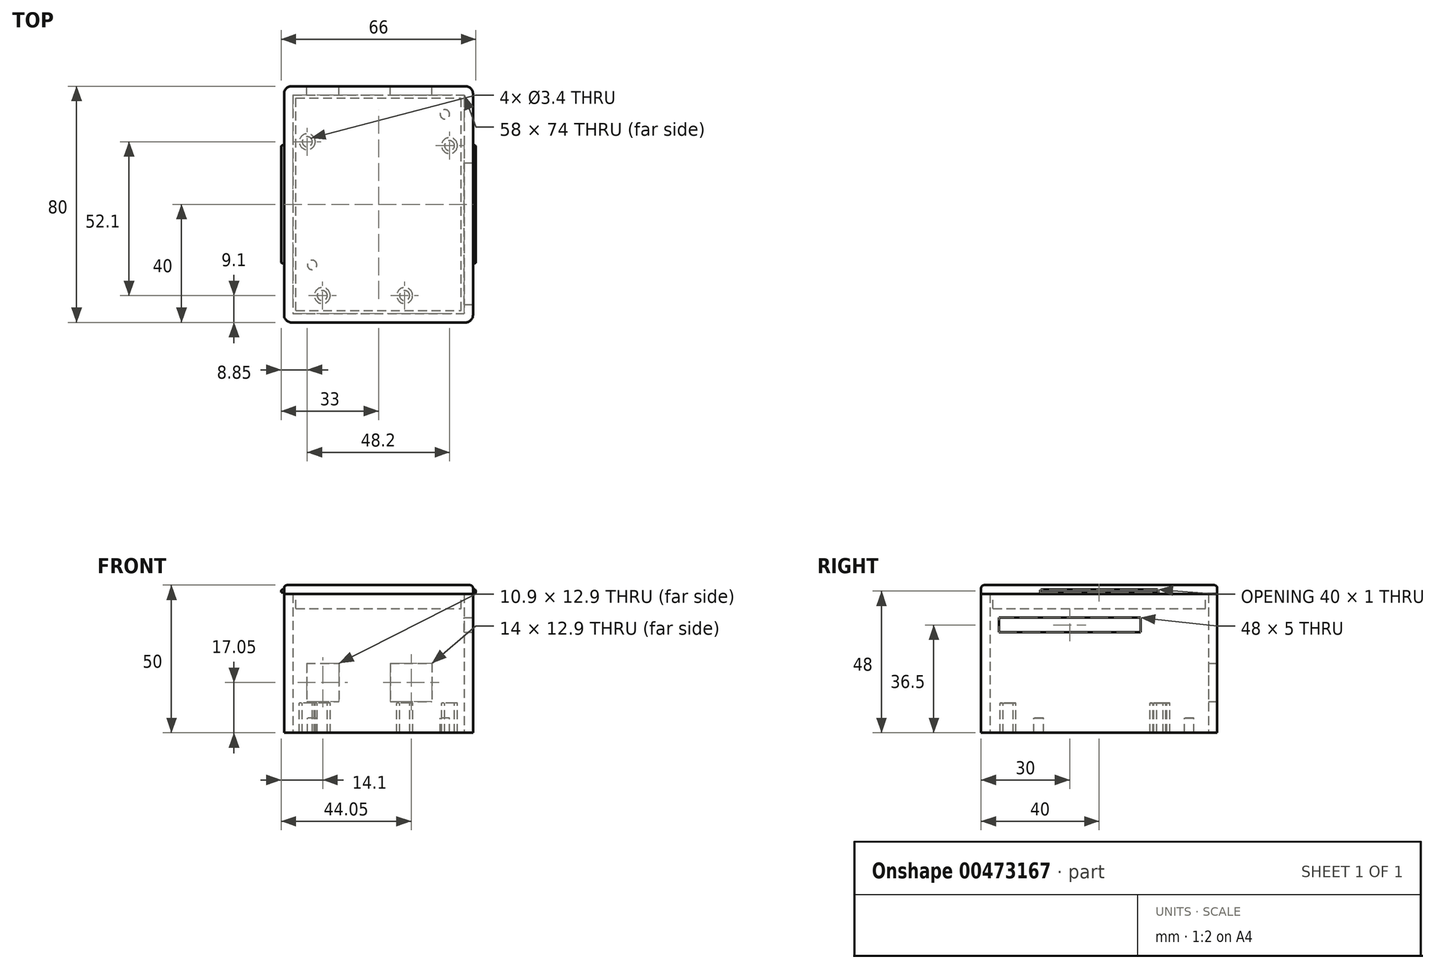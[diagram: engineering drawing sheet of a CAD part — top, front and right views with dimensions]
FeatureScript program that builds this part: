
annotation { "Feature Type Name" : "Feature", "Feature Type Description" : "" }
export const myFeature = defineFeature(function(context is Context, id is Id, definition is map)
    precondition{}
    {
        {
            var Q0;
            Q0=qCreatedBy(makeId("Top.planeOp"),FACE);
            var sketch = newSketch(context, id + "F0", { "sketchPlane" : qUnion([Q0])});
            skLineSegment(sketch, "E0.bottom", {"start": v(-32, 40) * mm, "end": v(32, 40) * mm});
            skLineSegment(sketch, "E0.top", {"start": v(-32, -40) * mm, "end": v(32, -40) * mm});
            skLineSegment(sketch, "E0.left", {"start": v(-32, 40) * mm, "end": v(-32, -40) * mm});
            skLineSegment(sketch, "E0.right", {"start": v(32, 40) * mm, "end": v(32, -40) * mm});
            skPoint(sketch, "E0.middle", {"position": v(0, 0) * mm});
            skSolve(sketch);
        }
        {
            var Q0;
            Q0=makeQuery(id+"F0.imprint","IMPRINT",FACE,{"disambiguationData":[TD([[makeQuery(id+"F0.imprint","IMPRINT",EDGE,{"derivedFrom":sQuery(id+"F0.wireOp",EDGE,"E0.bottom")}),-1.0]])]});
            extrude(context, id + "F1", {"entities" : qUnion([Q0]), "depth" : 45 * mm});
        }
        {
            var Q0;
            Q0=makeQuery(id+"F1.opExtrude","CAP_FACE",FACE,{"disambiguationData":[OSD([sQuery(id+"F0.wireOp",EDGE,"E0.bottom"),sQuery(id+"F0.wireOp",EDGE,"E0.top"),sQuery(id+"F0.wireOp",EDGE,"E0.left"),sQuery(id+"F0.wireOp",EDGE,"E0.right")])],"isStart":false});
            shell(context, id + "F2", {"entities" : qUnion([Q0]), "thickness" : 3 * mm});
        }
        {
            var Q0;
            Q0=makeQuery(id+"F1.opExtrude","CAP_FACE",FACE,{"disambiguationData":[OSD([sQuery(id+"F0.wireOp",EDGE,"E0.bottom"),sQuery(id+"F0.wireOp",EDGE,"E0.top"),sQuery(id+"F0.wireOp",EDGE,"E0.left"),sQuery(id+"F0.wireOp",EDGE,"E0.right")])],"isStart":true});
            extrude(context, id + "F3", {"entities" : qUnion([Q0]), "operationType" : NewBodyOperationType.ADD, "depth" : 2 * mm});
        }
        {
            var Q0;
            Q0=makeQuery(id+"F1.opExtrude","CAP_FACE",FACE,{"disambiguationData":[OSD([sQuery(id+"F0.wireOp",EDGE,"E0.bottom"),sQuery(id+"F0.wireOp",EDGE,"E0.top"),sQuery(id+"F0.wireOp",EDGE,"E0.left"),sQuery(id+"F0.wireOp",EDGE,"E0.right")])],"isStart":false});
            var sketch = newSketch(context, id + "F4", { "sketchPlane" : qUnion([Q0])});
            skLineSegment(sketch, "E1.bottom", {"start": v(-32, 40) * mm, "end": v(32, 40) * mm});
            skLineSegment(sketch, "E1.top", {"start": v(-32, -40) * mm, "end": v(32, -40) * mm});
            skLineSegment(sketch, "E1.left", {"start": v(-32, 40) * mm, "end": v(-32, -40) * mm});
            skLineSegment(sketch, "E1.right", {"start": v(32, 40) * mm, "end": v(32, -40) * mm});
            skLineSegment(sketch, "E2.bottom", {"start": v(-28, -36) * mm, "end": v(28, -36) * mm});
            skLineSegment(sketch, "E2.top", {"start": v(-28, 36) * mm, "end": v(28, 36) * mm});
            skLineSegment(sketch, "E2.left", {"start": v(-28, -36) * mm, "end": v(-28, 36) * mm});
            skLineSegment(sketch, "E2.right", {"start": v(28, -36) * mm, "end": v(28, 36) * mm});
            skPoint(sketch, "E2.middle", {"position": v(0, 0) * mm});
            skSolve(sketch);
        }
        {
            var Q0;
            Q0=makeQuery(id+"F4.imprint","IMPRINT",FACE,{"disambiguationData":[TD([[makeQuery(id+"F4.imprint","IMPRINT",EDGE,{"derivedFrom":sQuery(id+"F4.wireOp",EDGE,"E1.bottom")}),-1.0]])]});
            var Q1;
            Q1=makeQuery(id+"F4.imprint","IMPRINT",FACE,{"disambiguationData":[TD([[makeQuery(id+"F4.imprint","IMPRINT",EDGE,{"derivedFrom":sQuery(id+"F4.wireOp",EDGE,"E2.bottom")}),-1.0]])]});
            var Q2;
            Q2=makeQuery(id+"F4.imprint","IMPRINT",FACE,{"disambiguationData":[TD([[makeQuery(id+"F4.imprint","IMPRINT",EDGE,{"derivedFrom":sQuery(id+"F4.wireOp",EDGE,"E2.bottom")}),1.0]])]});
            extrude(context, id + "F5", {"entities" : qUnion([Q0, Q1, Q2]), "depth" : 3 * mm});
        }
        {
            var Q0;
            Q0=makeQuery(id+"F4.imprint","IMPRINT",FACE,{"disambiguationData":[TD([[makeQuery(id+"F4.imprint","IMPRINT",EDGE,{"derivedFrom":sQuery(id+"F4.wireOp",EDGE,"E2.bottom")}),1.0]])]});
            extrude(context, id + "F6", {"entities" : qUnion([Q0]), "operationType" : NewBodyOperationType.ADD, "oppositeDirection" : true, "depth" : 5 * mm, "offsetDistance" : 25 * mm});
        }
        {
            var Q0;
            Q0=makeQuery(id+"F2.opShell","OFFSET_FACE",FACE,{"disambiguationData":[OSD([sQuery(id+"F0.wireOp",EDGE,"E0.bottom"),sQuery(id+"F0.wireOp",EDGE,"E0.top"),sQuery(id+"F0.wireOp",EDGE,"E0.left"),sQuery(id+"F0.wireOp",EDGE,"E0.right")])]});
            var sketch = newSketch(context, id + "F7", { "sketchPlane" : qUnion([Q0])});
            skCircle(sketch, "E3", {"center": v(8.85, -30.9) * mm, "radius": 1.7 * mm});
            skCircle(sketch, "E4", {"center": v(-19.05, -30.9) * mm, "radius": 1.7 * mm});
            skCircle(sketch, "E5", {"center": v(-24.15, 21.2) * mm, "radius": 1.7 * mm});
            skCircle(sketch, "E6", {"center": v(24.05, 19.9) * mm, "radius": 1.7 * mm});
            skCircle(sketch, "E7", {"center": v(-24.15, 21.2) * mm, "radius": 2.7 * mm});
            skCircle(sketch, "E8", {"center": v(24.05, 19.9) * mm, "radius": 2.7 * mm});
            skCircle(sketch, "E9", {"center": v(-19.05, -30.9) * mm, "radius": 2.7 * mm});
            skCircle(sketch, "E10", {"center": v(8.85, -30.9) * mm, "radius": 2.7 * mm});
            skCircle(sketch, "E11", {"center": v(22.5, -20.5) * mm, "radius": 1.6 * mm});
            skCircle(sketch, "E12.MirrorC", {"center": v(-22.5, -20.5) * mm, "radius": 1.6 * mm});
            skCircle(sketch, "E13", {"center": v(-22.5, 30.5) * mm, "radius": 1.6 * mm});
            skCircle(sketch, "E14.MirrorC", {"center": v(22.5, 30.5) * mm, "radius": 1.6 * mm});
            skLineSegment(sketch, "E15", {"start": v(24.05, 19.9) * mm, "end": v(-4.37, 19.9) * mm, "construction": true});
            skLineSegment(sketch, "E16", {"start": v(-24.15, 21.2) * mm, "end": v(-24.15, -16.15) * mm, "construction": true});
            skLineSegment(sketch, "E17", {"start": v(8.85, -30.9) * mm, "end": v(8.85, -1.88) * mm, "construction": true});
            skSolve(sketch);
        }
        {
            var Q0;
            Q0=makeQuery(id+"F7.imprint","IMPRINT",FACE,{"disambiguationData":[TD([[makeQuery(id+"F7.imprint","IMPRINT",EDGE,{"derivedFrom":sQuery(id+"F7.wireOp",EDGE,"E3")}),-1.0]])]});
            var Q1;
            Q1=makeQuery(id+"F7.imprint","IMPRINT",FACE,{"disambiguationData":[TD([[makeQuery(id+"F7.imprint","IMPRINT",EDGE,{"derivedFrom":sQuery(id+"F7.wireOp",EDGE,"E4")}),-1.0]])]});
            var Q2;
            Q2=makeQuery(id+"F7.imprint","IMPRINT",FACE,{"disambiguationData":[TD([[makeQuery(id+"F7.imprint","IMPRINT",EDGE,{"derivedFrom":sQuery(id+"F7.wireOp",EDGE,"E5")}),-1.0]])]});
            var Q3;
            Q3=makeQuery(id+"F7.imprint","IMPRINT",FACE,{"disambiguationData":[TD([[makeQuery(id+"F7.imprint","IMPRINT",EDGE,{"derivedFrom":sQuery(id+"F7.wireOp",EDGE,"E6")}),-1.0]])]});
            extrude(context, id + "F8", {"entities" : qUnion([Q0, Q1, Q2, Q3]), "operationType" : NewBodyOperationType.ADD, "depth" : 5 * mm});
        }
        {
            var Q0;
            Q0=makeQuery(id+"F8.boolean.opBoolean","SPLIT",FACE,{"disambiguationData":[TD([makeQuery(id+"F8.opExtrude","SWEPT_FACE",FACE,{"disambiguationData":[OSD([sQuery(id+"F7.wireOp",EDGE,"E5")])]})])],"derivedFrom":makeQuery(id+"F2.opShell","OFFSET_FACE",FACE,{"disambiguationData":[OSD([sQuery(id+"F0.wireOp",EDGE,"E0.bottom"),sQuery(id+"F0.wireOp",EDGE,"E0.top"),sQuery(id+"F0.wireOp",EDGE,"E0.left"),sQuery(id+"F0.wireOp",EDGE,"E0.right")])]})});
            var Q1;
            Q1=makeQuery(id+"F8.boolean.opBoolean","SPLIT",FACE,{"disambiguationData":[TD([makeQuery(id+"F8.opExtrude","SWEPT_FACE",FACE,{"disambiguationData":[OSD([sQuery(id+"F7.wireOp",EDGE,"E6")])]})])],"derivedFrom":makeQuery(id+"F2.opShell","OFFSET_FACE",FACE,{"disambiguationData":[OSD([sQuery(id+"F0.wireOp",EDGE,"E0.bottom"),sQuery(id+"F0.wireOp",EDGE,"E0.top"),sQuery(id+"F0.wireOp",EDGE,"E0.left"),sQuery(id+"F0.wireOp",EDGE,"E0.right")])]})});
            var Q2;
            Q2=makeQuery(id+"F8.boolean.opBoolean","SPLIT",FACE,{"disambiguationData":[TD([makeQuery(id+"F8.opExtrude","SWEPT_FACE",FACE,{"disambiguationData":[OSD([sQuery(id+"F7.wireOp",EDGE,"E3")])]})])],"derivedFrom":makeQuery(id+"F2.opShell","OFFSET_FACE",FACE,{"disambiguationData":[OSD([sQuery(id+"F0.wireOp",EDGE,"E0.bottom"),sQuery(id+"F0.wireOp",EDGE,"E0.top"),sQuery(id+"F0.wireOp",EDGE,"E0.left"),sQuery(id+"F0.wireOp",EDGE,"E0.right")])]})});
            var Q3;
            Q3=makeQuery(id+"F8.boolean.opBoolean","SPLIT",FACE,{"disambiguationData":[TD([makeQuery(id+"F8.opExtrude","SWEPT_FACE",FACE,{"disambiguationData":[OSD([sQuery(id+"F7.wireOp",EDGE,"E4")])]})])],"derivedFrom":makeQuery(id+"F2.opShell","OFFSET_FACE",FACE,{"disambiguationData":[OSD([sQuery(id+"F0.wireOp",EDGE,"E0.bottom"),sQuery(id+"F0.wireOp",EDGE,"E0.top"),sQuery(id+"F0.wireOp",EDGE,"E0.left"),sQuery(id+"F0.wireOp",EDGE,"E0.right")])]})});
            var Q4;
            Q4=makeQuery(id+"F7.imprint","IMPRINT",FACE,{"disambiguationData":[TD([[makeQuery(id+"F7.imprint","IMPRINT",EDGE,{"derivedFrom":sQuery(id+"F7.wireOp",EDGE,"E13")}),1.0]])]});
            var Q5;
            Q5=makeQuery(id+"F7.imprint","IMPRINT",FACE,{"disambiguationData":[TD([[makeQuery(id+"F7.imprint","IMPRINT",EDGE,{"derivedFrom":sQuery(id+"F7.wireOp",EDGE,"E14.MirrorC")}),-1.0]])]});
            var Q6;
            Q6=makeQuery(id+"F7.imprint","IMPRINT",FACE,{"disambiguationData":[TD([[makeQuery(id+"F7.imprint","IMPRINT",EDGE,{"derivedFrom":sQuery(id+"F7.wireOp",EDGE,"E11")}),1.0]])]});
            var Q7;
            Q7=makeQuery(id+"F7.imprint","IMPRINT",FACE,{"disambiguationData":[TD([[makeQuery(id+"F7.imprint","IMPRINT",EDGE,{"derivedFrom":sQuery(id+"F7.wireOp",EDGE,"E12.MirrorC")}),-1.0]])]});
            extrude(context, id + "F9", {"entities" : qUnion([Q0, Q1, Q2, Q3, Q4, Q5, Q6, Q7]), "operationType" : NewBodyOperationType.REMOVE, "oppositeDirection" : true, "depth" : 5 * mm});
        }
        {
            var Q0;
            Q0=makeQuery(id+"F3.opExtrude","CAP_FACE",FACE,{"disambiguationData":[OSD([sQuery(id+"F0.wireOp",EDGE,"E0.bottom"),sQuery(id+"F0.wireOp",EDGE,"E0.top"),sQuery(id+"F0.wireOp",EDGE,"E0.left"),sQuery(id+"F0.wireOp",EDGE,"E0.right")])],"isStart":false});
            var sketch = newSketch(context, id + "F10", { "sketchPlane" : qUnion([Q0])});
            skCircle(sketch, "E18", {"center": v(-19.05, 30.9) * mm, "radius": 2.73 * mm});
            skCircle(sketch, "E19", {"center": v(8.85, 30.9) * mm, "radius": 2.73 * mm});
            skCircle(sketch, "E20.cCircle", {"center": v(-19.05, 30.9) * mm, "radius": 2.73 * mm, "construction": true});
            skLineSegment(sketch, "E20.0", {"start": v(-17.48, 28.17) * mm, "end": v(-20.63, 28.17) * mm});
            skLineSegment(sketch, "E20.1", {"start": v(-20.63, 28.17) * mm, "end": v(-22.2, 30.9) * mm});
            skLineSegment(sketch, "E20.2", {"start": v(-22.2, 30.9) * mm, "end": v(-20.63, 33.63) * mm});
            skLineSegment(sketch, "E20.3", {"start": v(-20.63, 33.63) * mm, "end": v(-17.48, 33.63) * mm});
            skLineSegment(sketch, "E20.4", {"start": v(-17.48, 33.63) * mm, "end": v(-15.9, 30.9) * mm});
            skLineSegment(sketch, "E20.5", {"start": v(-15.9, 30.9) * mm, "end": v(-17.48, 28.17) * mm});
            skPoint(sketch, "E20.0.midPoint", {"position": v(-19.05, 28.17) * mm});
            skCircle(sketch, "E21.cCircle", {"center": v(8.85, 30.9) * mm, "radius": 2.73 * mm, "construction": true});
            skLineSegment(sketch, "E21.0", {"start": v(10.42, 28.17) * mm, "end": v(7.27, 28.17) * mm});
            skLineSegment(sketch, "E21.1", {"start": v(7.27, 28.17) * mm, "end": v(5.7, 30.9) * mm});
            skLineSegment(sketch, "E21.2", {"start": v(5.7, 30.9) * mm, "end": v(7.27, 33.63) * mm});
            skLineSegment(sketch, "E21.3", {"start": v(7.27, 33.63) * mm, "end": v(10.42, 33.63) * mm});
            skLineSegment(sketch, "E21.4", {"start": v(10.42, 33.63) * mm, "end": v(12, 30.9) * mm});
            skLineSegment(sketch, "E21.5", {"start": v(12, 30.9) * mm, "end": v(10.42, 28.17) * mm});
            skPoint(sketch, "E21.0.midPoint", {"position": v(8.85, 28.17) * mm});
            skCircle(sketch, "E22", {"center": v(-24.15, -21.2) * mm, "radius": 2.73 * mm});
            skCircle(sketch, "E23", {"center": v(24.05, -19.9) * mm, "radius": 2.73 * mm});
            skCircle(sketch, "E24.cCircle", {"center": v(-24.15, -21.2) * mm, "radius": 2.73 * mm, "construction": true});
            skLineSegment(sketch, "E24.0", {"start": v(-22.58, -23.93) * mm, "end": v(-25.73, -23.93) * mm});
            skLineSegment(sketch, "E24.1", {"start": v(-25.73, -23.93) * mm, "end": v(-27.3, -21.2) * mm});
            skLineSegment(sketch, "E24.2", {"start": v(-27.3, -21.2) * mm, "end": v(-25.73, -18.47) * mm});
            skLineSegment(sketch, "E24.3", {"start": v(-25.73, -18.47) * mm, "end": v(-22.58, -18.47) * mm});
            skLineSegment(sketch, "E24.4", {"start": v(-22.58, -18.47) * mm, "end": v(-21, -21.2) * mm});
            skLineSegment(sketch, "E24.5", {"start": v(-21, -21.2) * mm, "end": v(-22.58, -23.93) * mm});
            skPoint(sketch, "E24.0.midPoint", {"position": v(-24.15, -23.93) * mm});
            skCircle(sketch, "E25.cCircle", {"center": v(24.05, -19.9) * mm, "radius": 2.73 * mm, "construction": true});
            skLineSegment(sketch, "E25.0", {"start": v(25.62, -22.63) * mm, "end": v(22.47, -22.63) * mm});
            skLineSegment(sketch, "E25.1", {"start": v(22.47, -22.63) * mm, "end": v(20.9, -19.9) * mm});
            skLineSegment(sketch, "E25.2", {"start": v(20.9, -19.9) * mm, "end": v(22.47, -17.17) * mm});
            skLineSegment(sketch, "E25.3", {"start": v(22.47, -17.17) * mm, "end": v(25.62, -17.17) * mm});
            skLineSegment(sketch, "E25.4", {"start": v(25.62, -17.17) * mm, "end": v(27.2, -19.9) * mm});
            skLineSegment(sketch, "E25.5", {"start": v(27.2, -19.9) * mm, "end": v(25.62, -22.63) * mm});
            skPoint(sketch, "E25.0.midPoint", {"position": v(24.05, -22.63) * mm});
            skSolve(sketch);
        }
        {
            var Q0;
            Q0=makeQuery(id+"F10.imprint","IMPRINT",FACE,{"disambiguationData":[TD([[makeQuery(id+"F10.imprint","IMPRINT",EDGE,{"derivedFrom":makeQuery(id+"F9.boolean.opBoolean","COPY",EDGE,{"derivedFrom":makeQuery(id+"F9.opExtrude","CAP_EDGE",EDGE,{"disambiguationData":[OSD([sQuery(id+"F7.wireOp",EDGE,"E4")])],"isStart":false})})}),1.0]])]});
            var Q1;
            {var subQ0=sQuery(id+"F10.wireOp",EDGE,"E20.3");var subQ1=sQuery(id+"F10.wireOp",EDGE,"E18");var subQ2=makeQuery(id+"F10.imprint","INTERSECT",VERTEX,{"derivedFrom":[subQ1,subQ0]});Q1=makeQuery(id+"F10.imprint","IMPRINT",FACE,{"disambiguationData":[TD([[makeQuery(id+"F10.imprint","IMPRINT",EDGE,{"disambiguationData":[TD([[subQ2,-1.0]])],"derivedFrom":subQ1}),-1.0]])]});}
            var Q2;
            {var subQ0=sQuery(id+"F10.wireOp",EDGE,"E20.2");var subQ1=sQuery(id+"F10.wireOp",EDGE,"E18");var subQ2=makeQuery(id+"F10.imprint","INTERSECT",VERTEX,{"derivedFrom":[subQ1,subQ0]});Q2=makeQuery(id+"F10.imprint","IMPRINT",FACE,{"disambiguationData":[TD([[makeQuery(id+"F10.imprint","IMPRINT",EDGE,{"disambiguationData":[TD([[subQ2,-1.0]])],"derivedFrom":subQ1}),-1.0]])]});}
            var Q3;
            {var subQ0=sQuery(id+"F10.wireOp",EDGE,"E20.1");var subQ1=sQuery(id+"F10.wireOp",EDGE,"E18");var subQ2=makeQuery(id+"F10.imprint","INTERSECT",VERTEX,{"derivedFrom":[subQ1,subQ0]});Q3=makeQuery(id+"F10.imprint","IMPRINT",FACE,{"disambiguationData":[TD([[makeQuery(id+"F10.imprint","IMPRINT",EDGE,{"disambiguationData":[TD([[subQ2,-1.0]])],"derivedFrom":subQ1}),-1.0]])]});}
            var Q4;
            {var subQ0=sQuery(id+"F10.wireOp",EDGE,"E20.0");var subQ1=sQuery(id+"F10.wireOp",EDGE,"E18");var subQ2=makeQuery(id+"F10.imprint","INTERSECT",VERTEX,{"derivedFrom":[subQ1,subQ0]});Q4=makeQuery(id+"F10.imprint","IMPRINT",FACE,{"disambiguationData":[TD([[makeQuery(id+"F10.imprint","IMPRINT",EDGE,{"disambiguationData":[TD([[subQ2,-1.0]])],"derivedFrom":subQ1}),-1.0]])]});}
            var Q5;
            {var subQ0=sQuery(id+"F10.wireOp",EDGE,"E20.4");var subQ1=sQuery(id+"F10.wireOp",EDGE,"E18");var subQ2=makeQuery(id+"F10.imprint","INTERSECT",VERTEX,{"derivedFrom":[subQ1,subQ0]});Q5=makeQuery(id+"F10.imprint","IMPRINT",FACE,{"disambiguationData":[TD([[makeQuery(id+"F10.imprint","IMPRINT",EDGE,{"disambiguationData":[TD([[subQ2,1.0]])],"derivedFrom":subQ1}),-1.0]])]});}
            var Q6;
            {var subQ0=sQuery(id+"F10.wireOp",EDGE,"E20.3");var subQ1=sQuery(id+"F10.wireOp",EDGE,"E18");var subQ2=makeQuery(id+"F10.imprint","INTERSECT",VERTEX,{"derivedFrom":[subQ1,subQ0]});Q6=makeQuery(id+"F10.imprint","IMPRINT",FACE,{"disambiguationData":[TD([[makeQuery(id+"F10.imprint","IMPRINT",EDGE,{"disambiguationData":[TD([[subQ2,1.0]])],"derivedFrom":subQ1}),-1.0]])]});}
            var Q7;
            Q7=makeQuery(id+"F10.imprint","IMPRINT",FACE,{"disambiguationData":[TD([[makeQuery(id+"F10.imprint","IMPRINT",EDGE,{"derivedFrom":makeQuery(id+"F9.boolean.opBoolean","COPY",EDGE,{"derivedFrom":makeQuery(id+"F9.opExtrude","CAP_EDGE",EDGE,{"disambiguationData":[OSD([sQuery(id+"F7.wireOp",EDGE,"E3")])],"isStart":false})})}),1.0]])]});
            var Q8;
            {var subQ0=sQuery(id+"F10.wireOp",EDGE,"E21.3");var subQ1=sQuery(id+"F10.wireOp",EDGE,"E19");var subQ2=makeQuery(id+"F10.imprint","INTERSECT",VERTEX,{"derivedFrom":[subQ1,subQ0]});Q8=makeQuery(id+"F10.imprint","IMPRINT",FACE,{"disambiguationData":[TD([[makeQuery(id+"F10.imprint","IMPRINT",EDGE,{"disambiguationData":[TD([[subQ2,-1.0]])],"derivedFrom":subQ1}),-1.0]])]});}
            var Q9;
            {var subQ0=sQuery(id+"F10.wireOp",EDGE,"E21.2");var subQ1=sQuery(id+"F10.wireOp",EDGE,"E19");var subQ2=makeQuery(id+"F10.imprint","INTERSECT",VERTEX,{"derivedFrom":[subQ1,subQ0]});Q9=makeQuery(id+"F10.imprint","IMPRINT",FACE,{"disambiguationData":[TD([[makeQuery(id+"F10.imprint","IMPRINT",EDGE,{"disambiguationData":[TD([[subQ2,-1.0]])],"derivedFrom":subQ1}),-1.0]])]});}
            var Q10;
            {var subQ0=sQuery(id+"F10.wireOp",EDGE,"E21.1");var subQ1=sQuery(id+"F10.wireOp",EDGE,"E19");var subQ2=makeQuery(id+"F10.imprint","INTERSECT",VERTEX,{"derivedFrom":[subQ1,subQ0]});Q10=makeQuery(id+"F10.imprint","IMPRINT",FACE,{"disambiguationData":[TD([[makeQuery(id+"F10.imprint","IMPRINT",EDGE,{"disambiguationData":[TD([[subQ2,-1.0]])],"derivedFrom":subQ1}),-1.0]])]});}
            var Q11;
            {var subQ0=sQuery(id+"F10.wireOp",EDGE,"E21.0");var subQ1=sQuery(id+"F10.wireOp",EDGE,"E19");var subQ2=makeQuery(id+"F10.imprint","INTERSECT",VERTEX,{"derivedFrom":[subQ1,subQ0]});Q11=makeQuery(id+"F10.imprint","IMPRINT",FACE,{"disambiguationData":[TD([[makeQuery(id+"F10.imprint","IMPRINT",EDGE,{"disambiguationData":[TD([[subQ2,-1.0]])],"derivedFrom":subQ1}),-1.0]])]});}
            var Q12;
            {var subQ0=sQuery(id+"F10.wireOp",EDGE,"E21.4");var subQ1=sQuery(id+"F10.wireOp",EDGE,"E19");var subQ2=makeQuery(id+"F10.imprint","INTERSECT",VERTEX,{"derivedFrom":[subQ1,subQ0]});Q12=makeQuery(id+"F10.imprint","IMPRINT",FACE,{"disambiguationData":[TD([[makeQuery(id+"F10.imprint","IMPRINT",EDGE,{"disambiguationData":[TD([[subQ2,1.0]])],"derivedFrom":subQ1}),-1.0]])]});}
            var Q13;
            {var subQ0=sQuery(id+"F10.wireOp",EDGE,"E21.3");var subQ1=sQuery(id+"F10.wireOp",EDGE,"E19");var subQ2=makeQuery(id+"F10.imprint","INTERSECT",VERTEX,{"derivedFrom":[subQ1,subQ0]});Q13=makeQuery(id+"F10.imprint","IMPRINT",FACE,{"disambiguationData":[TD([[makeQuery(id+"F10.imprint","IMPRINT",EDGE,{"disambiguationData":[TD([[subQ2,1.0]])],"derivedFrom":subQ1}),-1.0]])]});}
            var Q14;
            Q14=makeQuery(id+"F10.imprint","IMPRINT",FACE,{"disambiguationData":[TD([[makeQuery(id+"F10.imprint","IMPRINT",EDGE,{"derivedFrom":makeQuery(id+"F9.boolean.opBoolean","COPY",EDGE,{"derivedFrom":makeQuery(id+"F9.opExtrude","CAP_EDGE",EDGE,{"disambiguationData":[OSD([sQuery(id+"F7.wireOp",EDGE,"E5")])],"isStart":false})})}),1.0]])]});
            var Q15;
            {var subQ0=sQuery(id+"F10.wireOp",EDGE,"E24.2");var subQ1=sQuery(id+"F10.wireOp",EDGE,"E22");var subQ2=makeQuery(id+"F10.imprint","INTERSECT",VERTEX,{"derivedFrom":[subQ1,subQ0]});Q15=makeQuery(id+"F10.imprint","IMPRINT",FACE,{"disambiguationData":[TD([[makeQuery(id+"F10.imprint","IMPRINT",EDGE,{"disambiguationData":[TD([[subQ2,-1.0]])],"derivedFrom":subQ1}),-1.0]])]});}
            var Q16;
            {var subQ0=sQuery(id+"F10.wireOp",EDGE,"E24.3");var subQ1=sQuery(id+"F10.wireOp",EDGE,"E22");var subQ2=makeQuery(id+"F10.imprint","INTERSECT",VERTEX,{"derivedFrom":[subQ1,subQ0]});Q16=makeQuery(id+"F10.imprint","IMPRINT",FACE,{"disambiguationData":[TD([[makeQuery(id+"F10.imprint","IMPRINT",EDGE,{"disambiguationData":[TD([[subQ2,-1.0]])],"derivedFrom":subQ1}),-1.0]])]});}
            var Q17;
            {var subQ0=sQuery(id+"F10.wireOp",EDGE,"E24.3");var subQ1=sQuery(id+"F10.wireOp",EDGE,"E22");var subQ2=makeQuery(id+"F10.imprint","INTERSECT",VERTEX,{"derivedFrom":[subQ1,subQ0]});Q17=makeQuery(id+"F10.imprint","IMPRINT",FACE,{"disambiguationData":[TD([[makeQuery(id+"F10.imprint","IMPRINT",EDGE,{"disambiguationData":[TD([[subQ2,1.0]])],"derivedFrom":subQ1}),-1.0]])]});}
            var Q18;
            {var subQ0=sQuery(id+"F10.wireOp",EDGE,"E24.4");var subQ1=sQuery(id+"F10.wireOp",EDGE,"E22");var subQ2=makeQuery(id+"F10.imprint","INTERSECT",VERTEX,{"derivedFrom":[subQ1,subQ0]});Q18=makeQuery(id+"F10.imprint","IMPRINT",FACE,{"disambiguationData":[TD([[makeQuery(id+"F10.imprint","IMPRINT",EDGE,{"disambiguationData":[TD([[subQ2,1.0]])],"derivedFrom":subQ1}),-1.0]])]});}
            var Q19;
            {var subQ0=sQuery(id+"F10.wireOp",EDGE,"E24.0");var subQ1=sQuery(id+"F10.wireOp",EDGE,"E22");var subQ2=makeQuery(id+"F10.imprint","INTERSECT",VERTEX,{"derivedFrom":[subQ1,subQ0]});Q19=makeQuery(id+"F10.imprint","IMPRINT",FACE,{"disambiguationData":[TD([[makeQuery(id+"F10.imprint","IMPRINT",EDGE,{"disambiguationData":[TD([[subQ2,-1.0]])],"derivedFrom":subQ1}),-1.0]])]});}
            var Q20;
            {var subQ0=sQuery(id+"F10.wireOp",EDGE,"E24.1");var subQ1=sQuery(id+"F10.wireOp",EDGE,"E22");var subQ2=makeQuery(id+"F10.imprint","INTERSECT",VERTEX,{"derivedFrom":[subQ1,subQ0]});Q20=makeQuery(id+"F10.imprint","IMPRINT",FACE,{"disambiguationData":[TD([[makeQuery(id+"F10.imprint","IMPRINT",EDGE,{"disambiguationData":[TD([[subQ2,-1.0]])],"derivedFrom":subQ1}),-1.0]])]});}
            var Q21;
            Q21=makeQuery(id+"F10.imprint","IMPRINT",FACE,{"disambiguationData":[TD([[makeQuery(id+"F10.imprint","IMPRINT",EDGE,{"derivedFrom":makeQuery(id+"F9.boolean.opBoolean","COPY",EDGE,{"derivedFrom":makeQuery(id+"F9.opExtrude","CAP_EDGE",EDGE,{"disambiguationData":[OSD([sQuery(id+"F7.wireOp",EDGE,"E6")])],"isStart":false})})}),1.0]])]});
            var Q22;
            {var subQ0=sQuery(id+"F10.wireOp",EDGE,"E25.2");var subQ1=sQuery(id+"F10.wireOp",EDGE,"E23");var subQ2=makeQuery(id+"F10.imprint","INTERSECT",VERTEX,{"derivedFrom":[subQ1,subQ0]});Q22=makeQuery(id+"F10.imprint","IMPRINT",FACE,{"disambiguationData":[TD([[makeQuery(id+"F10.imprint","IMPRINT",EDGE,{"disambiguationData":[TD([[subQ2,-1.0]])],"derivedFrom":subQ1}),-1.0]])]});}
            var Q23;
            {var subQ0=sQuery(id+"F10.wireOp",EDGE,"E25.3");var subQ1=sQuery(id+"F10.wireOp",EDGE,"E23");var subQ2=makeQuery(id+"F10.imprint","INTERSECT",VERTEX,{"derivedFrom":[subQ1,subQ0]});Q23=makeQuery(id+"F10.imprint","IMPRINT",FACE,{"disambiguationData":[TD([[makeQuery(id+"F10.imprint","IMPRINT",EDGE,{"disambiguationData":[TD([[subQ2,-1.0]])],"derivedFrom":subQ1}),-1.0]])]});}
            var Q24;
            {var subQ0=sQuery(id+"F10.wireOp",EDGE,"E25.3");var subQ1=sQuery(id+"F10.wireOp",EDGE,"E23");var subQ2=makeQuery(id+"F10.imprint","INTERSECT",VERTEX,{"derivedFrom":[subQ1,subQ0]});Q24=makeQuery(id+"F10.imprint","IMPRINT",FACE,{"disambiguationData":[TD([[makeQuery(id+"F10.imprint","IMPRINT",EDGE,{"disambiguationData":[TD([[subQ2,1.0]])],"derivedFrom":subQ1}),-1.0]])]});}
            var Q25;
            {var subQ0=sQuery(id+"F10.wireOp",EDGE,"E25.4");var subQ1=sQuery(id+"F10.wireOp",EDGE,"E23");var subQ2=makeQuery(id+"F10.imprint","INTERSECT",VERTEX,{"derivedFrom":[subQ1,subQ0]});Q25=makeQuery(id+"F10.imprint","IMPRINT",FACE,{"disambiguationData":[TD([[makeQuery(id+"F10.imprint","IMPRINT",EDGE,{"disambiguationData":[TD([[subQ2,1.0]])],"derivedFrom":subQ1}),-1.0]])]});}
            var Q26;
            {var subQ0=sQuery(id+"F10.wireOp",EDGE,"E25.0");var subQ1=sQuery(id+"F10.wireOp",EDGE,"E23");var subQ2=makeQuery(id+"F10.imprint","INTERSECT",VERTEX,{"derivedFrom":[subQ1,subQ0]});Q26=makeQuery(id+"F10.imprint","IMPRINT",FACE,{"disambiguationData":[TD([[makeQuery(id+"F10.imprint","IMPRINT",EDGE,{"disambiguationData":[TD([[subQ2,-1.0]])],"derivedFrom":subQ1}),-1.0]])]});}
            var Q27;
            {var subQ0=sQuery(id+"F10.wireOp",EDGE,"E25.1");var subQ1=sQuery(id+"F10.wireOp",EDGE,"E23");var subQ2=makeQuery(id+"F10.imprint","INTERSECT",VERTEX,{"derivedFrom":[subQ1,subQ0]});Q27=makeQuery(id+"F10.imprint","IMPRINT",FACE,{"disambiguationData":[TD([[makeQuery(id+"F10.imprint","IMPRINT",EDGE,{"disambiguationData":[TD([[subQ2,-1.0]])],"derivedFrom":subQ1}),-1.0]])]});}
            extrude(context, id + "F11", {"entities" : qUnion([Q0, Q1, Q2, Q3, Q4, Q5, Q6, Q7, Q8, Q9, Q10, Q11, Q12, Q13, Q14, Q15, Q16, Q17, Q18, Q19, Q20, Q21, Q22, Q23, Q24, Q25, Q26, Q27]), "operationType" : NewBodyOperationType.REMOVE, "oppositeDirection" : true, "depth" : 2.6 * mm, "offsetDistance" : 25 * mm});
        }
        {
            var Q0;
            Q0=makeQuery(id+"F1.opExtrude","SWEPT_FACE",FACE,{"disambiguationData":[OSD([sQuery(id+"F0.wireOp",EDGE,"E0.bottom")])]});
            var sketch = newSketch(context, id + "F12", { "sketchPlane" : qUnion([Q0])});
            skLineSegment(sketch, "E26.bottom", {"start": v(24.35, 21.5) * mm, "end": v(13.45, 21.5) * mm});
            skLineSegment(sketch, "E26.top", {"start": v(24.35, 8.6) * mm, "end": v(13.45, 8.6) * mm});
            skLineSegment(sketch, "E26.left", {"start": v(24.35, 21.5) * mm, "end": v(24.35, 8.6) * mm});
            skLineSegment(sketch, "E26.right", {"start": v(13.45, 21.5) * mm, "end": v(13.45, 8.6) * mm});
            skPoint(sketch, "E26.middle", {"position": v(18.9, 15.05) * mm});
            skLineSegment(sketch, "E27.bottom", {"start": v(-4.05, 21.5) * mm, "end": v(-18.05, 21.5) * mm});
            skLineSegment(sketch, "E27.top", {"start": v(-4.05, 8.6) * mm, "end": v(-18.05, 8.6) * mm});
            skLineSegment(sketch, "E27.left", {"start": v(-4.05, 21.5) * mm, "end": v(-4.05, 8.6) * mm});
            skLineSegment(sketch, "E27.right", {"start": v(-18.05, 21.5) * mm, "end": v(-18.05, 8.6) * mm});
            skPoint(sketch, "E27.middle", {"position": v(-11.05, 15.05) * mm});
            skSolve(sketch);
        }
        {
            var Q0;
            Q0=makeQuery(id+"F12.imprint","IMPRINT",FACE,{"disambiguationData":[TD([[makeQuery(id+"F12.imprint","IMPRINT",EDGE,{"derivedFrom":sQuery(id+"F12.wireOp",EDGE,"E27.bottom")}),1.0]])]});
            var Q1;
            Q1=makeQuery(id+"F12.imprint","IMPRINT",FACE,{"disambiguationData":[TD([[makeQuery(id+"F12.imprint","IMPRINT",EDGE,{"derivedFrom":sQuery(id+"F12.wireOp",EDGE,"E26.bottom")}),1.0]])]});
            extrude(context, id + "F13", {"entities" : qUnion([Q0, Q1]), "operationType" : NewBodyOperationType.REMOVE, "oppositeDirection" : true, "depth" : 3 * mm});
        }
        {
            var Q0;
            Q0=makeQuery(id+"F1.opExtrude","SWEPT_FACE",FACE,{"disambiguationData":[OSD([sQuery(id+"F0.wireOp",EDGE,"E0.right")])]});
            var sketch = newSketch(context, id + "F14", { "sketchPlane" : qUnion([Q0])});
            skLineSegment(sketch, "E28.bottom", {"start": v(-34, 32) * mm, "end": v(14, 32) * mm});
            skLineSegment(sketch, "E28.top", {"start": v(-34, 37) * mm, "end": v(14, 37) * mm});
            skLineSegment(sketch, "E28.left", {"start": v(-34, 32) * mm, "end": v(-34, 37) * mm});
            skLineSegment(sketch, "E28.right", {"start": v(14, 32) * mm, "end": v(14, 37) * mm});
            skPoint(sketch, "E28.middle", {"position": v(-10, 34.5) * mm});
            skSolve(sketch);
        }
        {
            var Q0;
            Q0=makeQuery(id+"F14.imprint","IMPRINT",FACE,{"disambiguationData":[TD([[makeQuery(id+"F14.imprint","IMPRINT",EDGE,{"derivedFrom":sQuery(id+"F14.wireOp",EDGE,"E28.bottom")}),1.0]])]});
            extrude(context, id + "F15", {"entities" : qUnion([Q0]), "operationType" : NewBodyOperationType.REMOVE, "oppositeDirection" : true, "depth" : 3 * mm});
        }
        {
            var Q0;
            Q0=makeQuery(id+"F5.opExtrude","SWEPT_FACE",FACE,{"disambiguationData":[OSD([sQuery(id+"F4.wireOp",EDGE,"E1.right")])]});
            var sketch = newSketch(context, id + "F16", { "sketchPlane" : qUnion([Q0])});
            skLineSegment(sketch, "E29.bottom", {"start": v(-20, 46.5) * mm, "end": v(20, 46.5) * mm});
            skLineSegment(sketch, "E29.top", {"start": v(-20, 45.5) * mm, "end": v(20, 45.5) * mm});
            skLineSegment(sketch, "E29.left", {"start": v(-20, 46.5) * mm, "end": v(-20, 45.5) * mm});
            skLineSegment(sketch, "E29.right", {"start": v(20, 46.5) * mm, "end": v(20, 45.5) * mm});
            skPoint(sketch, "E29.middle", {"position": v(0, 46) * mm});
            skSolve(sketch);
        }
        {
            var Q0;
            Q0=makeQuery(id+"F5.opExtrude","SWEPT_FACE",FACE,{"disambiguationData":[OSD([sQuery(id+"F4.wireOp",EDGE,"E1.left")])]});
            var sketch = newSketch(context, id + "F17", { "sketchPlane" : qUnion([Q0])});
            skLineSegment(sketch, "E30.bottom", {"start": v(-20, 45.5) * mm, "end": v(20, 45.5) * mm});
            skLineSegment(sketch, "E30.top", {"start": v(-20, 46.5) * mm, "end": v(20, 46.5) * mm});
            skLineSegment(sketch, "E30.left", {"start": v(-20, 45.5) * mm, "end": v(-20, 46.5) * mm});
            skLineSegment(sketch, "E30.right", {"start": v(20, 45.5) * mm, "end": v(20, 46.5) * mm});
            skPoint(sketch, "E30.middle", {"position": v(0, 46) * mm});
            skSolve(sketch);
        }
        {
            var Q0;
            Q0=makeQuery(id+"F16.imprint","IMPRINT",FACE,{"disambiguationData":[TD([[makeQuery(id+"F16.imprint","IMPRINT",EDGE,{"derivedFrom":sQuery(id+"F16.wireOp",EDGE,"E29.bottom")}),-1.0]])]});
            extrude(context, id + "F18", {"entities" : qUnion([Q0]), "operationType" : NewBodyOperationType.ADD, "depth" : 1 * mm});
        }
        {
            var Q0;
            Q0=makeQuery(id+"F17.imprint","IMPRINT",FACE,{"disambiguationData":[TD([[makeQuery(id+"F17.imprint","IMPRINT",EDGE,{"derivedFrom":sQuery(id+"F17.wireOp",EDGE,"E30.bottom")}),1.0]])]});
            extrude(context, id + "F19", {"entities" : qUnion([Q0]), "operationType" : NewBodyOperationType.ADD, "depth" : 1 * mm});
        }
        {
            var Q0;
            Q0=makeQuery(id+"F5.opExtrude","CAP_EDGE",EDGE,{"disambiguationData":[OSD([sQuery(id+"F4.wireOp",EDGE,"E1.right")])],"isStart":false});
            var Q1;
            Q1=makeQuery(id+"F5.opExtrude","CAP_EDGE",EDGE,{"disambiguationData":[OSD([sQuery(id+"F4.wireOp",EDGE,"E1.top")])],"isStart":false});
            var Q2;
            Q2=makeQuery(id+"F5.opExtrude","CAP_EDGE",EDGE,{"disambiguationData":[OSD([sQuery(id+"F4.wireOp",EDGE,"E1.left")])],"isStart":false});
            var Q3;
            Q3=makeQuery(id+"F5.opExtrude","CAP_EDGE",EDGE,{"disambiguationData":[OSD([sQuery(id+"F4.wireOp",EDGE,"E1.bottom")])],"isStart":false});
            fillet(context, id + "F20", {"entities" : qUnion([Q0, Q1, Q2, Q3]), "radius" : 1 * mm, "tangentPropagation" : true, "allowEdgeOverflow" : false});
        }
        {
            var Q0;
            Q0=makeQuery(id+"F19.opExtrude","CAP_EDGE",EDGE,{"disambiguationData":[OSD([sQuery(id+"F17.wireOp",EDGE,"E30.top")])],"isStart":false});
            var Q1;
            Q1=makeQuery(id+"F19.opExtrude","SWEPT_EDGE",EDGE,{"disambiguationData":[OSD([sQuery(id+"F17.wireOp",EDGE,"E30.top"),sQuery(id+"F17.wireOp",EDGE,"E30.left")])]});
            var Q2;
            Q2=makeQuery(id+"F19.opExtrude","SWEPT_EDGE",EDGE,{"disambiguationData":[OSD([sQuery(id+"F17.wireOp",EDGE,"E30.top"),sQuery(id+"F17.wireOp",EDGE,"E30.right")])]});
            var Q3;
            Q3=makeQuery(id+"F18.opExtrude","SWEPT_EDGE",EDGE,{"disambiguationData":[OSD([sQuery(id+"F16.wireOp",EDGE,"E29.bottom"),sQuery(id+"F16.wireOp",EDGE,"E29.left")])]});
            var Q4;
            Q4=makeQuery(id+"F18.opExtrude","CAP_EDGE",EDGE,{"disambiguationData":[OSD([sQuery(id+"F16.wireOp",EDGE,"E29.bottom")])],"isStart":false});
            var Q5;
            Q5=makeQuery(id+"F18.opExtrude","SWEPT_EDGE",EDGE,{"disambiguationData":[OSD([sQuery(id+"F16.wireOp",EDGE,"E29.bottom"),sQuery(id+"F16.wireOp",EDGE,"E29.right")])]});
            var Q6;
            Q6=makeQuery(id+"F19.opExtrude","CAP_EDGE",EDGE,{"disambiguationData":[OSD([sQuery(id+"F17.wireOp",EDGE,"E30.left")])],"isStart":false});
            var Q7;
            Q7=makeQuery(id+"F19.opExtrude","CAP_EDGE",EDGE,{"disambiguationData":[OSD([sQuery(id+"F17.wireOp",EDGE,"E30.right")])],"isStart":false});
            var Q8;
            Q8=makeQuery(id+"F18.opExtrude","CAP_EDGE",EDGE,{"disambiguationData":[OSD([sQuery(id+"F16.wireOp",EDGE,"E29.left")])],"isStart":false});
            var Q9;
            Q9=makeQuery(id+"F18.opExtrude","CAP_EDGE",EDGE,{"disambiguationData":[OSD([sQuery(id+"F16.wireOp",EDGE,"E29.right")])],"isStart":false});
            fillet(context, id + "F21", {"entities" : qUnion([Q0, Q1, Q2, Q3, Q4, Q5, Q6, Q7, Q8, Q9]), "radius" : .5 * mm, "tangentPropagation" : true, "allowEdgeOverflow" : false});
        }
        {
            var Q0;
            {var subQ0=sQuery(id+"F0.wireOp",EDGE,"E0.right");var subQ1=sQuery(id+"F0.wireOp",EDGE,"E0.top");Q0=makeQuery(id+"F3.boolean.opBoolean","MERGE",EDGE,{"derivedFrom":[makeQuery(id+"F1.opExtrude","SWEPT_EDGE",EDGE,{"disambiguationData":[OSD([subQ1,subQ0])]}),makeQuery(id+"F3.opExtrude","SWEPT_EDGE",EDGE,{"disambiguationData":[OSD([subQ1,subQ0])]})]});}
            var Q1;
            Q1=makeQuery(id+"F5.opExtrude","SWEPT_EDGE",EDGE,{"disambiguationData":[OSD([sQuery(id+"F4.wireOp",EDGE,"E1.top"),sQuery(id+"F4.wireOp",EDGE,"E1.right")])]});
            var Q2;
            {var subQ0=sQuery(id+"F0.wireOp",EDGE,"E0.left");var subQ1=sQuery(id+"F0.wireOp",EDGE,"E0.top");Q2=makeQuery(id+"F3.boolean.opBoolean","MERGE",EDGE,{"derivedFrom":[makeQuery(id+"F1.opExtrude","SWEPT_EDGE",EDGE,{"disambiguationData":[OSD([subQ1,subQ0])]}),makeQuery(id+"F3.opExtrude","SWEPT_EDGE",EDGE,{"disambiguationData":[OSD([subQ1,subQ0])]})]});}
            var Q3;
            Q3=makeQuery(id+"F5.opExtrude","SWEPT_EDGE",EDGE,{"disambiguationData":[OSD([sQuery(id+"F4.wireOp",EDGE,"E1.top"),sQuery(id+"F4.wireOp",EDGE,"E1.left")])]});
            var Q4;
            Q4=makeQuery(id+"F5.opExtrude","SWEPT_EDGE",EDGE,{"disambiguationData":[OSD([sQuery(id+"F4.wireOp",EDGE,"E1.bottom"),sQuery(id+"F4.wireOp",EDGE,"E1.right")])]});
            var Q5;
            {var subQ0=sQuery(id+"F0.wireOp",EDGE,"E0.right");var subQ1=sQuery(id+"F0.wireOp",EDGE,"E0.bottom");Q5=makeQuery(id+"F3.boolean.opBoolean","MERGE",EDGE,{"derivedFrom":[makeQuery(id+"F1.opExtrude","SWEPT_EDGE",EDGE,{"disambiguationData":[OSD([subQ1,subQ0])]}),makeQuery(id+"F3.opExtrude","SWEPT_EDGE",EDGE,{"disambiguationData":[OSD([subQ1,subQ0])]})]});}
            var Q6;
            Q6=makeQuery(id+"F5.opExtrude","SWEPT_EDGE",EDGE,{"disambiguationData":[OSD([sQuery(id+"F4.wireOp",EDGE,"E1.bottom"),sQuery(id+"F4.wireOp",EDGE,"E1.left")])]});
            var Q7;
            {var subQ0=sQuery(id+"F0.wireOp",EDGE,"E0.left");var subQ1=sQuery(id+"F0.wireOp",EDGE,"E0.bottom");Q7=makeQuery(id+"F3.boolean.opBoolean","MERGE",EDGE,{"derivedFrom":[makeQuery(id+"F1.opExtrude","SWEPT_EDGE",EDGE,{"disambiguationData":[OSD([subQ1,subQ0])]}),makeQuery(id+"F3.opExtrude","SWEPT_EDGE",EDGE,{"disambiguationData":[OSD([subQ1,subQ0])]})]});}
            fillet(context, id + "F22", {"entities" : qUnion([Q0, Q1, Q2, Q3, Q4, Q5, Q6, Q7]), "radius" : 2.5 * mm, "tangentPropagation" : true, "allowEdgeOverflow" : false});
        }
    });
